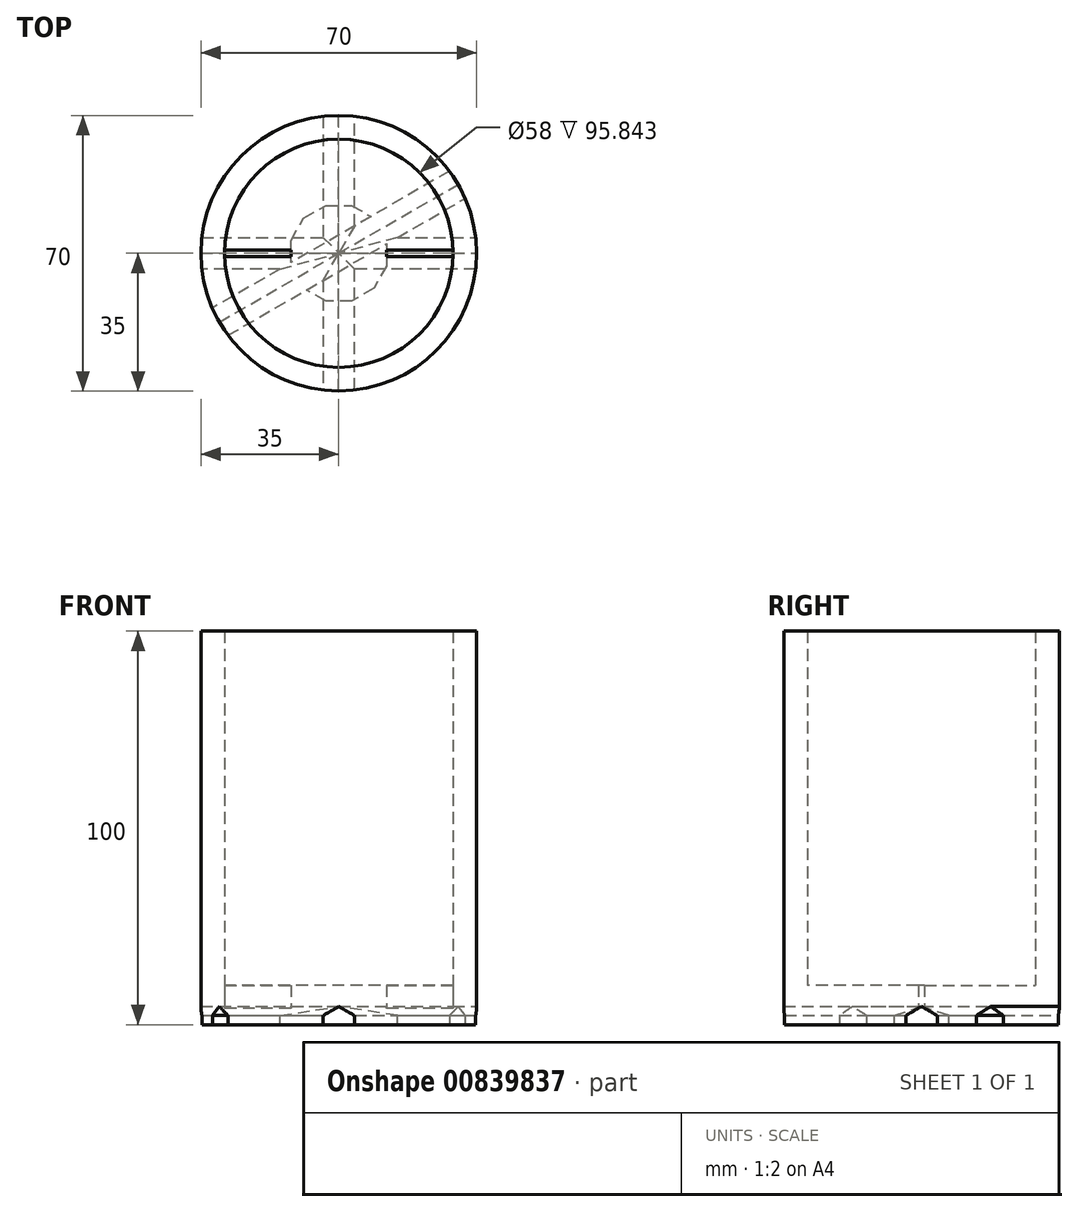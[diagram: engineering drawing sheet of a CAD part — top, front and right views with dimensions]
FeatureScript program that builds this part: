
annotation { "Feature Type Name" : "Feature", "Feature Type Description" : "" }
export const myFeature = defineFeature(function(context is Context, id is Id, definition is map)
    precondition{}
    {
        {
            var Q0;
            Q0=qCreatedBy(makeId("Top.planeOp"),FACE);
            var sketch = newSketch(context, id + "F0", { "sketchPlane" : qUnion([Q0])});
            skCircle(sketch, "E0", {"center": v(0, 0) * mm, "radius": 35 * mm});
            skCircle(sketch, "E1", {"center": v(0, 0) * mm, "radius": 29 * mm});
            skLineSegment(sketch, "E2.bottom", {"start": v(-35, 0.8) * mm, "end": v(35, 0.8) * mm});
            skLineSegment(sketch, "E2.top", {"start": v(-35, -0.8) * mm, "end": v(35, -0.8) * mm});
            skLineSegment(sketch, "E2.left", {"start": v(-35, 0.8) * mm, "end": v(-35, -0.8) * mm});
            skLineSegment(sketch, "E2.right", {"start": v(35, 0.8) * mm, "end": v(35, -0.8) * mm});
            skLineSegment(sketch, "E3.bottom", {"start": v(-0.8, 35) * mm, "end": v(0.8, 35) * mm});
            skLineSegment(sketch, "E3.top", {"start": v(-0.8, -35) * mm, "end": v(0.8, -35) * mm});
            skLineSegment(sketch, "E3.left", {"start": v(-0.8, 35) * mm, "end": v(-0.8, -35) * mm});
            skLineSegment(sketch, "E3.right", {"start": v(0.8, 35) * mm, "end": v(0.8, -35) * mm});
            skCircle(sketch, "E4.cCircle", {"center": v(0, 0) * mm, "radius": 35 * mm, "construction": true});
            skLineSegment(sketch, "E4.0", {"start": v(35, 11.37) * mm, "end": v(35, -11.37) * mm, "construction": true});
            skLineSegment(sketch, "E4.1", {"start": v(35, -11.37) * mm, "end": v(21.63, -29.76) * mm, "construction": true});
            skLineSegment(sketch, "E4.2", {"start": v(21.63, -29.76) * mm, "end": v(0, -36.8) * mm, "construction": true});
            skLineSegment(sketch, "E4.3", {"start": v(0, -36.8) * mm, "end": v(-21.63, -29.76) * mm, "construction": true});
            skLineSegment(sketch, "E4.4", {"start": v(-21.63, -29.76) * mm, "end": v(-35, -11.37) * mm, "construction": true});
            skLineSegment(sketch, "E4.5", {"start": v(-35, -11.37) * mm, "end": v(-35, 11.37) * mm, "construction": true});
            skLineSegment(sketch, "E4.6", {"start": v(-35, 11.37) * mm, "end": v(-21.63, 29.76) * mm, "construction": true});
            skLineSegment(sketch, "E4.7", {"start": v(-21.63, 29.76) * mm, "end": v(0, 36.8) * mm, "construction": true});
            skLineSegment(sketch, "E4.8", {"start": v(0, 36.8) * mm, "end": v(21.63, 29.76) * mm, "construction": true});
            skLineSegment(sketch, "E4.9", {"start": v(21.63, 29.76) * mm, "end": v(35, 11.37) * mm, "construction": true});
            skPoint(sketch, "E4.0.midPoint", {"position": v(35, 0) * mm});
            skCircle(sketch, "E5.cCircle", {"center": v(0, 0) * mm, "radius": 12.16 * mm, "construction": true});
            skLineSegment(sketch, "E5.0", {"start": v(3.26, -12.16) * mm, "end": v(-3.26, -12.16) * mm});
            skLineSegment(sketch, "E5.1", {"start": v(-3.26, -12.16) * mm, "end": v(-8.9, -8.9) * mm});
            skLineSegment(sketch, "E5.2", {"start": v(-8.9, -8.9) * mm, "end": v(-12.16, -3.26) * mm});
            skLineSegment(sketch, "E5.3", {"start": v(-12.16, -3.26) * mm, "end": v(-12.16, 3.26) * mm});
            skLineSegment(sketch, "E5.4", {"start": v(-12.16, 3.26) * mm, "end": v(-8.9, 8.9) * mm});
            skLineSegment(sketch, "E5.5", {"start": v(-8.9, 8.9) * mm, "end": v(-3.26, 12.16) * mm});
            skLineSegment(sketch, "E5.6", {"start": v(-3.26, 12.16) * mm, "end": v(3.26, 12.16) * mm});
            skLineSegment(sketch, "E5.7", {"start": v(3.26, 12.16) * mm, "end": v(8.9, 8.9) * mm});
            skLineSegment(sketch, "E5.8", {"start": v(8.9, 8.9) * mm, "end": v(12.16, 3.26) * mm});
            skLineSegment(sketch, "E5.9", {"start": v(12.16, 3.26) * mm, "end": v(12.16, -3.26) * mm});
            skLineSegment(sketch, "E5.10", {"start": v(12.16, -3.26) * mm, "end": v(8.9, -8.9) * mm});
            skLineSegment(sketch, "E5.11", {"start": v(8.9, -8.9) * mm, "end": v(3.26, -12.16) * mm});
            skPoint(sketch, "E5.0.midPoint", {"position": v(0, -12.16) * mm});
            skSolve(sketch);
        }
        {
            var Q0;
            {var subQ0=sQuery(id+"F0.wireOp",EDGE,"E3.bottom");Q0=makeQuery(id+"F0.imprint","IMPRINT",FACE,{"disambiguationData":[TD([[makeQuery(id+"F0.imprint","IMPRINT",EDGE,{"derivedFrom":subQ0}),1.0]])]});}
            var Q1;
            {var subQ0=sQuery(id+"F0.wireOp",EDGE,"E2.left");Q1=makeQuery(id+"F0.imprint","IMPRINT",FACE,{"disambiguationData":[TD([[makeQuery(id+"F0.imprint","IMPRINT",EDGE,{"derivedFrom":subQ0}),-1.0]])]});}
            var Q2;
            {var subQ0=sQuery(id+"F0.wireOp",EDGE,"E3.top");Q2=makeQuery(id+"F0.imprint","IMPRINT",FACE,{"disambiguationData":[TD([[makeQuery(id+"F0.imprint","IMPRINT",EDGE,{"derivedFrom":subQ0}),-1.0]])]});}
            var Q3;
            {var subQ0=sQuery(id+"F0.wireOp",EDGE,"E2.right");Q3=makeQuery(id+"F0.imprint","IMPRINT",FACE,{"disambiguationData":[TD([[makeQuery(id+"F0.imprint","IMPRINT",EDGE,{"derivedFrom":subQ0}),1.0]])]});}
            var Q4;
            {var subQ3=sQuery(id+"F0.wireOp",EDGE,"E3.right");var subQ5=sQuery(id+"F0.wireOp",EDGE,"E1");var subQ7=makeQuery(id+"F0.imprint","INTERSECT",VERTEX,{"disambiguationData":[OD(0.0)],"derivedFrom":[subQ5,subQ3]});Q4=makeQuery(id+"F0.imprint","IMPRINT",FACE,{"disambiguationData":[TD([[makeQuery(id+"F0.imprint","IMPRINT",EDGE,{"disambiguationData":[TD([[subQ7,1.0]])],"derivedFrom":subQ5}),-1.0]])]});}
            var Q5;
            {var subQ0=sQuery(id+"F0.wireOp",EDGE,"E2.top");var subQ5=sQuery(id+"F0.wireOp",EDGE,"E1");var subQ7=makeQuery(id+"F0.imprint","INTERSECT",VERTEX,{"disambiguationData":[OD(0.0)],"derivedFrom":[subQ5,subQ0]});Q5=makeQuery(id+"F0.imprint","IMPRINT",FACE,{"disambiguationData":[TD([[makeQuery(id+"F0.imprint","IMPRINT",EDGE,{"disambiguationData":[TD([[subQ7,-1.0]])],"derivedFrom":subQ5}),-1.0]])]});}
            var Q6;
            {var subQ3=sQuery(id+"F0.wireOp",EDGE,"E3.right");var subQ5=sQuery(id+"F0.wireOp",EDGE,"E1");var subQ6=makeQuery(id+"F0.imprint","INTERSECT",VERTEX,{"disambiguationData":[OD(1.0)],"derivedFrom":[subQ5,subQ3]});Q6=makeQuery(id+"F0.imprint","IMPRINT",FACE,{"disambiguationData":[TD([[makeQuery(id+"F0.imprint","IMPRINT",EDGE,{"disambiguationData":[TD([[subQ6,-1.0]])],"derivedFrom":subQ5}),-1.0]])]});}
            var Q7;
            {var subQ5=sQuery(id+"F0.wireOp",EDGE,"E3.bottom");Q7=makeQuery(id+"F0.imprint","IMPRINT",FACE,{"disambiguationData":[TD([[makeQuery(id+"F0.imprint","IMPRINT",EDGE,{"derivedFrom":subQ5}),-1.0]])]});}
            var Q8;
            {var subQ5=sQuery(id+"F0.wireOp",EDGE,"E2.left");Q8=makeQuery(id+"F0.imprint","IMPRINT",FACE,{"disambiguationData":[TD([[makeQuery(id+"F0.imprint","IMPRINT",EDGE,{"derivedFrom":subQ5}),1.0]])]});}
            var Q9;
            {var subQ5=sQuery(id+"F0.wireOp",EDGE,"E3.top");Q9=makeQuery(id+"F0.imprint","IMPRINT",FACE,{"disambiguationData":[TD([[makeQuery(id+"F0.imprint","IMPRINT",EDGE,{"derivedFrom":subQ5}),1.0]])]});}
            var Q10;
            {var subQ5=sQuery(id+"F0.wireOp",EDGE,"E2.right");Q10=makeQuery(id+"F0.imprint","IMPRINT",FACE,{"disambiguationData":[TD([[makeQuery(id+"F0.imprint","IMPRINT",EDGE,{"derivedFrom":subQ5}),-1.0]])]});}
            var Q11;
            {var subQ0=sQuery(id+"F0.wireOp",EDGE,"E3.left");var subQ1=sQuery(id+"F0.wireOp",EDGE,"E1");var subQ2=makeQuery(id+"F0.imprint","INTERSECT",VERTEX,{"disambiguationData":[OD(0.0)],"derivedFrom":[subQ1,subQ0]});Q11=makeQuery(id+"F0.imprint","IMPRINT",FACE,{"disambiguationData":[TD([[makeQuery(id+"F0.imprint","IMPRINT",EDGE,{"disambiguationData":[TD([[subQ2,-1.0]])],"derivedFrom":subQ1}),1.0]])]});}
            var Q12;
            {var subQ3=sQuery(id+"F0.wireOp",EDGE,"E3.left");var subQ5=sQuery(id+"F0.wireOp",EDGE,"E1");var subQ6=makeQuery(id+"F0.imprint","INTERSECT",VERTEX,{"disambiguationData":[OD(0.0)],"derivedFrom":[subQ5,subQ3]});Q12=makeQuery(id+"F0.imprint","IMPRINT",FACE,{"disambiguationData":[TD([[makeQuery(id+"F0.imprint","IMPRINT",EDGE,{"disambiguationData":[TD([[subQ6,-1.0]])],"derivedFrom":subQ5}),-1.0]])]});}
            var Q13;
            {var subQ0=sQuery(id+"F0.wireOp",EDGE,"E2.bottom");var subQ1=sQuery(id+"F0.wireOp",EDGE,"E1");var subQ2=makeQuery(id+"F0.imprint","INTERSECT",VERTEX,{"disambiguationData":[OD(1.0)],"derivedFrom":[subQ1,subQ0]});Q13=makeQuery(id+"F0.imprint","IMPRINT",FACE,{"disambiguationData":[TD([[makeQuery(id+"F0.imprint","IMPRINT",EDGE,{"disambiguationData":[TD([[subQ2,-1.0]])],"derivedFrom":subQ1}),1.0]])]});}
            var Q14;
            {var subQ0=sQuery(id+"F0.wireOp",EDGE,"E2.top");var subQ1=sQuery(id+"F0.wireOp",EDGE,"E1");var subQ2=makeQuery(id+"F0.imprint","INTERSECT",VERTEX,{"disambiguationData":[OD(0.0)],"derivedFrom":[subQ1,subQ0]});Q14=makeQuery(id+"F0.imprint","IMPRINT",FACE,{"disambiguationData":[TD([[makeQuery(id+"F0.imprint","IMPRINT",EDGE,{"disambiguationData":[TD([[subQ2,-1.0]])],"derivedFrom":subQ1}),1.0]])]});}
            var Q15;
            {var subQ0=sQuery(id+"F0.wireOp",EDGE,"E3.left");var subQ1=sQuery(id+"F0.wireOp",EDGE,"E1");var subQ2=makeQuery(id+"F0.imprint","INTERSECT",VERTEX,{"disambiguationData":[OD(1.0)],"derivedFrom":[subQ1,subQ0]});Q15=makeQuery(id+"F0.imprint","IMPRINT",FACE,{"disambiguationData":[TD([[makeQuery(id+"F0.imprint","IMPRINT",EDGE,{"disambiguationData":[TD([[subQ2,-1.0]])],"derivedFrom":subQ1}),1.0]])]});}
            var Q16;
            {var subQ0=sQuery(id+"F0.wireOp",EDGE,"E2.bottom");var subQ1=sQuery(id+"F0.wireOp",EDGE,"E1");var subQ2=makeQuery(id+"F0.imprint","INTERSECT",VERTEX,{"disambiguationData":[OD(0.0)],"derivedFrom":[subQ1,subQ0]});Q16=makeQuery(id+"F0.imprint","IMPRINT",FACE,{"disambiguationData":[TD([[makeQuery(id+"F0.imprint","IMPRINT",EDGE,{"disambiguationData":[TD([[subQ2,1.0]])],"derivedFrom":subQ1}),1.0]])]});}
            var Q17;
            {var subQ0=sQuery(id+"F0.wireOp",EDGE,"E3.left");var subQ1=sQuery(id+"F0.wireOp",EDGE,"E2.bottom");var subQ2=makeQuery(id+"F0.imprint","INTERSECT",VERTEX,{"derivedFrom":[subQ1,subQ0]});Q17=makeQuery(id+"F0.imprint","IMPRINT",FACE,{"disambiguationData":[TD([[makeQuery(id+"F0.imprint","IMPRINT",EDGE,{"disambiguationData":[TD([[subQ2,-1.0]])],"derivedFrom":subQ1}),-1.0]])]});}
            var Q18;
            {var subQ0=sQuery(id+"F0.wireOp",EDGE,"E3.right");var subQ1=sQuery(id+"F0.wireOp",EDGE,"E1");var subQ2=makeQuery(id+"F0.imprint","INTERSECT",VERTEX,{"disambiguationData":[OD(0.0)],"derivedFrom":[subQ1,subQ0]});Q18=makeQuery(id+"F0.imprint","IMPRINT",FACE,{"disambiguationData":[TD([[makeQuery(id+"F0.imprint","IMPRINT",EDGE,{"disambiguationData":[TD([[subQ2,-1.0]])],"derivedFrom":subQ1}),1.0]])]});}
            var Q19;
            {var subQ0=sQuery(id+"F0.wireOp",EDGE,"E3.right");var subQ1=sQuery(id+"F0.wireOp",EDGE,"E1");var subQ2=makeQuery(id+"F0.imprint","INTERSECT",VERTEX,{"disambiguationData":[OD(0.0)],"derivedFrom":[subQ1,subQ0]});Q19=makeQuery(id+"F0.imprint","IMPRINT",FACE,{"disambiguationData":[TD([[makeQuery(id+"F0.imprint","IMPRINT",EDGE,{"disambiguationData":[TD([[subQ2,1.0]])],"derivedFrom":subQ1}),1.0]])]});}
            var Q20;
            {var subQ0=sQuery(id+"F0.wireOp",EDGE,"E3.right");var subQ1=sQuery(id+"F0.wireOp",EDGE,"E1");var subQ2=makeQuery(id+"F0.imprint","INTERSECT",VERTEX,{"disambiguationData":[OD(1.0)],"derivedFrom":[subQ1,subQ0]});Q20=makeQuery(id+"F0.imprint","IMPRINT",FACE,{"disambiguationData":[TD([[makeQuery(id+"F0.imprint","IMPRINT",EDGE,{"disambiguationData":[TD([[subQ2,-1.0]])],"derivedFrom":subQ1}),1.0]])]});}
            var Q21;
            {var subQ0=sQuery(id+"F0.wireOp",EDGE,"E5.4");Q21=makeQuery(id+"F0.imprint","IMPRINT",FACE,{"disambiguationData":[TD([[makeQuery(id+"F0.imprint","IMPRINT",EDGE,{"derivedFrom":subQ0}),-1.0]])]});}
            var Q22;
            {var subQ0=sQuery(id+"F0.wireOp",EDGE,"E5.1");Q22=makeQuery(id+"F0.imprint","IMPRINT",FACE,{"disambiguationData":[TD([[makeQuery(id+"F0.imprint","IMPRINT",EDGE,{"derivedFrom":subQ0}),-1.0]])]});}
            var Q23;
            {var subQ4=sQuery(id+"F0.wireOp",EDGE,"E5.10");Q23=makeQuery(id+"F0.imprint","IMPRINT",FACE,{"disambiguationData":[TD([[makeQuery(id+"F0.imprint","IMPRINT",EDGE,{"derivedFrom":subQ4}),-1.0]])]});}
            var Q24;
            {var subQ0=sQuery(id+"F0.wireOp",EDGE,"E5.7");Q24=makeQuery(id+"F0.imprint","IMPRINT",FACE,{"disambiguationData":[TD([[makeQuery(id+"F0.imprint","IMPRINT",EDGE,{"derivedFrom":subQ0}),-1.0]])]});}
            var Q25;
            {var subQ0=sQuery(id+"F0.wireOp",EDGE,"E3.left");var subQ1=sQuery(id+"F0.wireOp",EDGE,"E2.bottom");var subQ2=makeQuery(id+"F0.imprint","INTERSECT",VERTEX,{"derivedFrom":[subQ1,subQ0]});Q25=makeQuery(id+"F0.imprint","IMPRINT",FACE,{"disambiguationData":[TD([[makeQuery(id+"F0.imprint","IMPRINT",EDGE,{"disambiguationData":[TD([[subQ2,-1.0]])],"derivedFrom":subQ1}),1.0]])]});}
            var Q26;
            {var subQ0=sQuery(id+"F0.wireOp",EDGE,"E5.3");var subQ1=sQuery(id+"F0.wireOp",EDGE,"E2.bottom");var subQ2=makeQuery(id+"F0.imprint","INTERSECT",VERTEX,{"derivedFrom":[subQ1,subQ0]});Q26=makeQuery(id+"F0.imprint","IMPRINT",FACE,{"disambiguationData":[TD([[makeQuery(id+"F0.imprint","IMPRINT",EDGE,{"disambiguationData":[TD([[subQ2,-1.0]])],"derivedFrom":subQ1}),-1.0]])]});}
            var Q27;
            {var subQ0=sQuery(id+"F0.wireOp",EDGE,"E3.left");var subQ1=sQuery(id+"F0.wireOp",EDGE,"E2.top");var subQ2=makeQuery(id+"F0.imprint","INTERSECT",VERTEX,{"derivedFrom":[subQ1,subQ0]});Q27=makeQuery(id+"F0.imprint","IMPRINT",FACE,{"disambiguationData":[TD([[makeQuery(id+"F0.imprint","IMPRINT",EDGE,{"disambiguationData":[TD([[subQ2,-1.0]])],"derivedFrom":subQ1}),-1.0]])]});}
            var Q28;
            {var subQ0=sQuery(id+"F0.wireOp",EDGE,"E3.right");var subQ1=sQuery(id+"F0.wireOp",EDGE,"E2.bottom");var subQ2=makeQuery(id+"F0.imprint","INTERSECT",VERTEX,{"derivedFrom":[subQ1,subQ0]});Q28=makeQuery(id+"F0.imprint","IMPRINT",FACE,{"disambiguationData":[TD([[makeQuery(id+"F0.imprint","IMPRINT",EDGE,{"disambiguationData":[TD([[subQ2,-1.0]])],"derivedFrom":subQ1}),-1.0]])]});}
            extrude(context, id + "F1", {"entities" : qUnion([Q0, Q1, Q2, Q3, Q4, Q5, Q6, Q7, Q8, Q9, Q10, Q11, Q12, Q13, Q14, Q15, Q16, Q17, Q18, Q19, Q20, Q21, Q22, Q23, Q24, Q25, Q26, Q27, Q28]), "depth" : 10 * mm, "offsetDistance" : 25 * mm});
        }
        {
            var Q0;
            Q0=qSketchRegion(id+"F0",true);
            extrude(context, id + "F2", {"entities" : qUnion([Q0]), "operationType" : NewBodyOperationType.ADD, "depth" : 100 * mm, "offsetDistance" : 25 * mm});
        }
        {
            var Q0;
            Q0=qCreatedBy(makeId("Front.planeOp"),FACE);
            var sketch = newSketch(context, id + "F3", { "sketchPlane" : qUnion([Q0])});
            skCircle(sketch, "E6.cCircle", {"center": v(0, 0) * mm, "radius": 4 * mm, "construction": true});
            skLineSegment(sketch, "E6.0", {"start": v(4, 2.3) * mm, "end": v(4, -2.3) * mm});
            skLineSegment(sketch, "E6.1", {"start": v(4, -2.3) * mm, "end": v(0, -4.62) * mm});
            skLineSegment(sketch, "E6.2", {"start": v(0, -4.62) * mm, "end": v(-4, -2.3) * mm});
            skLineSegment(sketch, "E6.3", {"start": v(-4, -2.3) * mm, "end": v(-4, 2.3) * mm});
            skLineSegment(sketch, "E6.4", {"start": v(-4, 2.3) * mm, "end": v(0, 4.62) * mm});
            skLineSegment(sketch, "E6.5", {"start": v(0, 4.62) * mm, "end": v(4, 2.3) * mm});
            skPoint(sketch, "E6.0.midPoint", {"position": v(4, 0) * mm});
            skLineSegment(sketch, "E7", {"start": v(0, 0) * mm, "end": v(0, 68.4) * mm, "construction": true});
            skSolve(sketch);
        }
        {
            var Q0;
            Q0=makeQuery(id+"F3.imprint","IMPRINT",FACE,{"disambiguationData":[TD([[makeQuery(id+"F3.imprint","IMPRINT",EDGE,{"derivedFrom":sQuery(id+"F3.wireOp",EDGE,"mThpvVhg-KTDp-94mD-2KTh-e2I57yjgVE0Y")}),1.0]])]});
            var Q1;
            Q1=makeQuery(id+"F3.imprint","IMPRINT",FACE,{"disambiguationData":[TD([[makeQuery(id+"F3.imprint","IMPRINT",EDGE,{"derivedFrom":sQuery(id+"F3.wireOp",EDGE,"E6.0")}),-1.0]])]});
            extrude(context, id + "F4", {"entities" : qUnion([Q0, Q1]), "operationType" : NewBodyOperationType.REMOVE, "endBound" : BoundingType.SYMMETRIC, "depth" : 200 * mm, "offsetDistance" : 25 * mm});
        }
        {
            var Q0;
            Q0=qCreatedBy(makeId("Right.planeOp"),FACE);
            var sketch = newSketch(context, id + "F5", { "sketchPlane" : qUnion([Q0])});
            skCircle(sketch, "E8.cCircle", {"center": v(0, 0) * mm, "radius": 4 * mm, "construction": true});
            skLineSegment(sketch, "E8.0", {"start": v(-4, -2.3) * mm, "end": v(-4, 2.3) * mm});
            skLineSegment(sketch, "E8.1", {"start": v(-4, 2.3) * mm, "end": v(0, 4.62) * mm});
            skLineSegment(sketch, "E8.2", {"start": v(0, 4.62) * mm, "end": v(4, 2.3) * mm});
            skLineSegment(sketch, "E8.3", {"start": v(4, 2.3) * mm, "end": v(4, -2.3) * mm});
            skLineSegment(sketch, "E8.4", {"start": v(4, -2.3) * mm, "end": v(0, -4.62) * mm});
            skLineSegment(sketch, "E8.5", {"start": v(0, -4.62) * mm, "end": v(-4, -2.3) * mm});
            skPoint(sketch, "E8.0.midPoint", {"position": v(-4, 0) * mm});
            skSolve(sketch);
        }
        {
            var Q0;
            Q0=qSketchRegion(id+"F5",true);
            extrude(context, id + "F6", {"entities" : qUnion([Q0]), "operationType" : NewBodyOperationType.REMOVE, "endBound" : BoundingType.SYMMETRIC, "oppositeDirection" : true, "depth" : 200 * mm, "offsetDistance" : 25 * mm});
        }
        {
            var Q0;
            {var subQ0=sQuery(id+"F0.wireOp",EDGE,"E5.1");Q0=makeQuery(id+"F0.imprint","IMPRINT",FACE,{"disambiguationData":[TD([[makeQuery(id+"F0.imprint","IMPRINT",EDGE,{"derivedFrom":subQ0}),-1.0]])]});}
            var Q1;
            {var subQ4=sQuery(id+"F0.wireOp",EDGE,"E5.10");Q1=makeQuery(id+"F0.imprint","IMPRINT",FACE,{"disambiguationData":[TD([[makeQuery(id+"F0.imprint","IMPRINT",EDGE,{"derivedFrom":subQ4}),-1.0]])]});}
            var Q2;
            {var subQ0=sQuery(id+"F0.wireOp",EDGE,"E5.7");Q2=makeQuery(id+"F0.imprint","IMPRINT",FACE,{"disambiguationData":[TD([[makeQuery(id+"F0.imprint","IMPRINT",EDGE,{"derivedFrom":subQ0}),-1.0]])]});}
            var Q3;
            {var subQ0=sQuery(id+"F0.wireOp",EDGE,"E5.4");Q3=makeQuery(id+"F0.imprint","IMPRINT",FACE,{"disambiguationData":[TD([[makeQuery(id+"F0.imprint","IMPRINT",EDGE,{"derivedFrom":subQ0}),-1.0]])]});}
            var Q4;
            {var subQ0=sQuery(id+"F0.wireOp",EDGE,"E5.3");var subQ1=sQuery(id+"F0.wireOp",EDGE,"E2.bottom");var subQ2=makeQuery(id+"F0.imprint","INTERSECT",VERTEX,{"derivedFrom":[subQ1,subQ0]});Q4=makeQuery(id+"F0.imprint","IMPRINT",FACE,{"disambiguationData":[TD([[makeQuery(id+"F0.imprint","IMPRINT",EDGE,{"disambiguationData":[TD([[subQ2,-1.0]])],"derivedFrom":subQ1}),-1.0]])]});}
            var Q5;
            {var subQ0=sQuery(id+"F0.wireOp",EDGE,"E3.right");var subQ1=sQuery(id+"F0.wireOp",EDGE,"E2.bottom");var subQ2=makeQuery(id+"F0.imprint","INTERSECT",VERTEX,{"derivedFrom":[subQ1,subQ0]});Q5=makeQuery(id+"F0.imprint","IMPRINT",FACE,{"disambiguationData":[TD([[makeQuery(id+"F0.imprint","IMPRINT",EDGE,{"disambiguationData":[TD([[subQ2,-1.0]])],"derivedFrom":subQ1}),-1.0]])]});}
            var Q6;
            {var subQ0=sQuery(id+"F0.wireOp",EDGE,"E3.left");var subQ1=sQuery(id+"F0.wireOp",EDGE,"E2.bottom");var subQ2=makeQuery(id+"F0.imprint","INTERSECT",VERTEX,{"derivedFrom":[subQ1,subQ0]});Q6=makeQuery(id+"F0.imprint","IMPRINT",FACE,{"disambiguationData":[TD([[makeQuery(id+"F0.imprint","IMPRINT",EDGE,{"disambiguationData":[TD([[subQ2,-1.0]])],"derivedFrom":subQ1}),1.0]])]});}
            var Q7;
            {var subQ0=sQuery(id+"F0.wireOp",EDGE,"E3.left");var subQ1=sQuery(id+"F0.wireOp",EDGE,"E2.top");var subQ2=makeQuery(id+"F0.imprint","INTERSECT",VERTEX,{"derivedFrom":[subQ1,subQ0]});Q7=makeQuery(id+"F0.imprint","IMPRINT",FACE,{"disambiguationData":[TD([[makeQuery(id+"F0.imprint","IMPRINT",EDGE,{"disambiguationData":[TD([[subQ2,-1.0]])],"derivedFrom":subQ1}),-1.0]])]});}
            extrude(context, id + "F7", {"entities" : qUnion([Q0, Q1, Q2, Q3, Q4, Q5, Q6, Q7]), "depth" : 0.01 * mm, "offsetDistance" : 25 * mm});
        }
        {
            var Q0;
            Q0=makeQuery(id+"F7.opExtrude","SWEPT_FACE",FACE,{"disambiguationData":[OSD([sQuery(id+"F0.wireOp",EDGE,"E5.2")])]});
            var sketch = newSketch(context, id + "F8", { "sketchPlane" : qUnion([Q0])});
            skCircle(sketch, "E9.cCircle", {"center": v(0, 0) * mm, "radius": 4 * mm, "construction": true});
            skLineSegment(sketch, "E9.0", {"start": v(4, 2.3) * mm, "end": v(4, -2.3) * mm});
            skLineSegment(sketch, "E9.1", {"start": v(4, -2.3) * mm, "end": v(0, -4.62) * mm});
            skLineSegment(sketch, "E9.2", {"start": v(0, -4.62) * mm, "end": v(-4, -2.3) * mm});
            skLineSegment(sketch, "E9.3", {"start": v(-4, -2.3) * mm, "end": v(-4, 2.3) * mm});
            skLineSegment(sketch, "E9.4", {"start": v(-4, 2.3) * mm, "end": v(0, 4.62) * mm});
            skLineSegment(sketch, "E9.5", {"start": v(0, 4.62) * mm, "end": v(4, 2.3) * mm});
            skPoint(sketch, "E9.0.midPoint", {"position": v(4, 0) * mm});
            skSolve(sketch);
        }
        {
            var Q0;
            Q0 = qSketchRegion(id + "F8", true);
            extrude(context, id + "F9", {"entities" : qUnion([Q0]), "operationType" : NewBodyOperationType.REMOVE, "endBound" : BoundingType.SYMMETRIC, "depth" : 200 * mm, "offsetDistance" : 25 * mm});
        }
    });
